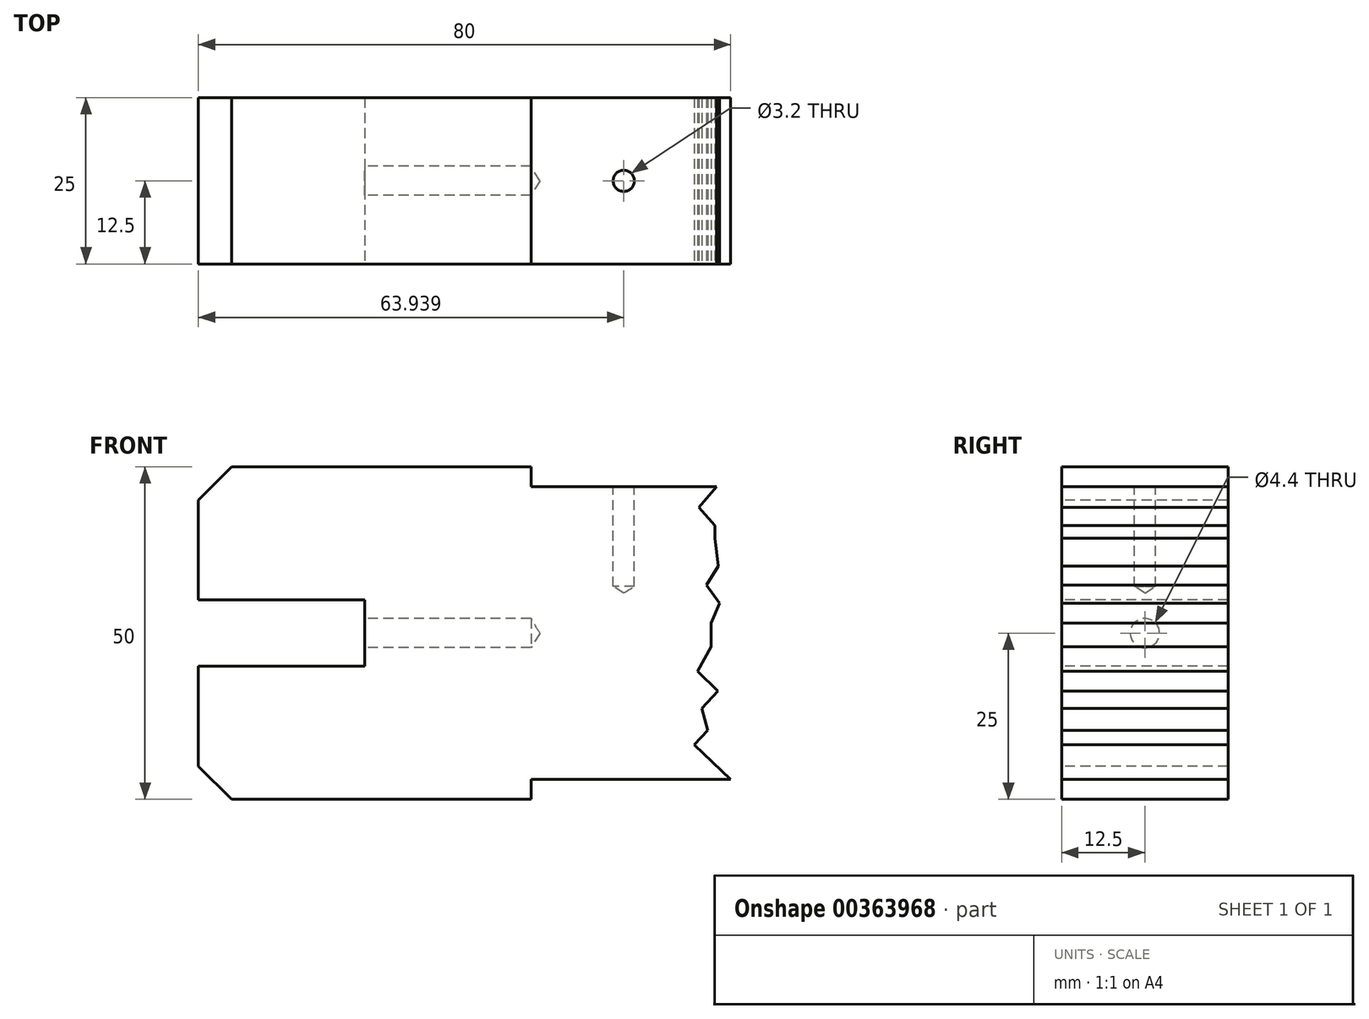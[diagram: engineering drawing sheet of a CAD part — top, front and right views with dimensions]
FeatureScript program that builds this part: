
annotation { "Feature Type Name" : "Feature", "Feature Type Description" : "" }
export const myFeature = defineFeature(function(context is Context, id is Id, definition is map)
    precondition{}
    {
        {
            var Q0;
            Q0=qCreatedBy(makeId("Front.planeOp"),FACE);
            var sketch = newSketch(context, id + "F0", { "sketchPlane" : qUnion([Q0])});
            skLineSegment(sketch, "E0.bottom", {"start": v(40, -25) * mm, "end": v(-40, -25) * mm});
            skLineSegment(sketch, "E0.top", {"start": v(40, 25) * mm, "end": v(-40, 25) * mm});
            skLineSegment(sketch, "E0.left", {"start": v(40, -25) * mm, "end": v(40, 25) * mm});
            skLineSegment(sketch, "E0.right", {"start": v(-40, -25) * mm, "end": v(-40, 25) * mm});
            skPoint(sketch, "E0.middle", {"position": v(0, 0) * mm});
            skSolve(sketch);
        }
        {
            var Q0;
            Q0=makeQuery(id+"F0.imprint","IMPRINT",FACE,{"disambiguationData":[TD([[makeQuery(id+"F0.imprint","IMPRINT",EDGE,{"derivedFrom":sQuery(id+"F0.wireOp",EDGE,"E0.bottom")}),-1.0]])]});
            extrude(context, id + "F1", {"entities" : qUnion([Q0]), "depth" : 25 * mm});
        }
        {
            var Q0;
            Q0=makeQuery(id+"F1.opExtrude","CAP_FACE",FACE,{"disambiguationData":[OSD([sQuery(id+"F0.wireOp",EDGE,"E0.bottom"),sQuery(id+"F0.wireOp",EDGE,"E0.top"),sQuery(id+"F0.wireOp",EDGE,"E0.left"),sQuery(id+"F0.wireOp",EDGE,"E0.right")])],"isStart":false});
            var sketch = newSketch(context, id + "F2", { "sketchPlane" : qUnion([Q0])});
            skLineSegment(sketch, "E1", {"start": v(-35, 25) * mm, "end": v(-40, 20) * mm});
            skLineSegment(sketch, "E2", {"start": v(-40, 20) * mm, "end": v(-40, 25) * mm});
            skLineSegment(sketch, "E3", {"start": v(-40, 25) * mm, "end": v(-35, 25) * mm});
            skLineSegment(sketch, "E4", {"start": v(-35, -25) * mm, "end": v(-40, -25) * mm});
            skLineSegment(sketch, "E5", {"start": v(-40, -25) * mm, "end": v(-40, -20) * mm});
            skLineSegment(sketch, "E6", {"start": v(-40, -20) * mm, "end": v(-35, -25) * mm});
            skSolve(sketch);
        }
        {
            var Q0;
            Q0=makeQuery(id+"F2.imprint","IMPRINT",FACE,{"disambiguationData":[TD([[makeQuery(id+"F2.imprint","IMPRINT",EDGE,{"derivedFrom":sQuery(id+"F2.wireOp",EDGE,"E4")}),-1.0]])]});
            var Q1;
            Q1=makeQuery(id+"F2.imprint","IMPRINT",FACE,{"disambiguationData":[TD([[makeQuery(id+"F2.imprint","IMPRINT",EDGE,{"derivedFrom":sQuery(id+"F2.wireOp",EDGE,"E1")}),-1.0]])]});
            extrude(context, id + "F3", {"entities" : qUnion([Q0, Q1]), "operationType" : NewBodyOperationType.REMOVE, "oppositeDirection" : true, "depth" : 25 * mm});
        }
        {
            var Q0;
            Q0=makeQuery(id+"F1.opExtrude","CAP_FACE",FACE,{"disambiguationData":[OSD([sQuery(id+"F0.wireOp",EDGE,"E0.bottom"),sQuery(id+"F0.wireOp",EDGE,"E0.top"),sQuery(id+"F0.wireOp",EDGE,"E0.left"),sQuery(id+"F0.wireOp",EDGE,"E0.right")])],"isStart":false});
            var sketch = newSketch(context, id + "F4", { "sketchPlane" : qUnion([Q0])});
            skLineSegment(sketch, "E7", {"start": v(-40, 5) * mm, "end": v(-15, 5) * mm});
            skLineSegment(sketch, "E8", {"start": v(-15, 5) * mm, "end": v(-15, -5) * mm});
            skLineSegment(sketch, "E9", {"start": v(-15, -5) * mm, "end": v(-40, -5) * mm});
            skLineSegment(sketch, "E10", {"start": v(-40, -5) * mm, "end": v(-40, 5) * mm});
            skSolve(sketch);
        }
        {
            var Q0;
            Q0=makeQuery(id+"F4.imprint","IMPRINT",FACE,{"disambiguationData":[TD([[makeQuery(id+"F4.imprint","IMPRINT",EDGE,{"derivedFrom":sQuery(id+"F4.wireOp",EDGE,"E7")}),-1.0]])]});
            extrude(context, id + "F5", {"entities" : qUnion([Q0]), "operationType" : NewBodyOperationType.REMOVE, "oppositeDirection" : true, "depth" : 25 * mm});
        }
        {
            var Q0;
            Q0=makeQuery(id+"F5.boolean.opBoolean","COPY",FACE,{"derivedFrom":makeQuery(id+"F5.opExtrude","SWEPT_FACE",FACE,{"disambiguationData":[OSD([sQuery(id+"F4.wireOp",EDGE,"E8")])]})});
            var sketch = newSketch(context, id + "F6", { "sketchPlane" : qUnion([Q0])});
            skPoint(sketch, "E11", {"position": v(12.5, 0) * mm});
            skSolve(sketch);
        }
        {
            var Q0;
            Q0=sQuery(id+"F6.wireOp",VERTEX,"E11");
            var Q1;
            Q1=makeQuery(id+"F1.opExtrude","SWEPT_BODY",BODY,{"disambiguationData":[OSD([sQuery(id+"F0.wireOp",EDGE,"E0.bottom"),sQuery(id+"F0.wireOp",EDGE,"E0.top"),sQuery(id+"F0.wireOp",EDGE,"E0.left"),sQuery(id+"F0.wireOp",EDGE,"E0.right")])]});
            hole(context, id + "F7", {"style" : HoleStyle.SIMPLE, "endStyle" : HoleEndStyle.BLIND, "standardTappedOrClearance" : lookupTablePath({ "fit" : "Normal", "standard" : "ISO", "size" : "M4", "type" : "Clearance" }), "standardBlindInLast" : lookupTablePath({ "fit" : "Standard", "standard" : "ISO", "size" : "M4", "type" : "Clearance" }), "holeDiameter" : 4.4 * mm, "holeDepth" : 25 * mm, "isTappedThrough" : true, "tappedDepth" : 12 * mm, "tapClearance" : 3, "locations" : qUnion([Q0]), "scope" : qUnion([Q1])});
        }
        {
            var Q0;
            Q0=makeQuery(id+"F1.opExtrude","CAP_FACE",FACE,{"disambiguationData":[OSD([sQuery(id+"F0.wireOp",EDGE,"E0.bottom"),sQuery(id+"F0.wireOp",EDGE,"E0.top"),sQuery(id+"F0.wireOp",EDGE,"E0.left"),sQuery(id+"F0.wireOp",EDGE,"E0.right")])],"isStart":false});
            var sketch = newSketch(context, id + "F8", { "sketchPlane" : qUnion([Q0])});
            skLineSegment(sketch, "E12", {"start": v(10, 25) * mm, "end": v(10, 22) * mm});
            skLineSegment(sketch, "E13", {"start": v(10, 22) * mm, "end": v(40, 22) * mm});
            skLineSegment(sketch, "E14", {"start": v(40, 22) * mm, "end": v(40, 25) * mm});
            skLineSegment(sketch, "E15", {"start": v(40, 25) * mm, "end": v(10, 25) * mm});
            skLineSegment(sketch, "E16", {"start": v(10, -25) * mm, "end": v(10, -22) * mm});
            skLineSegment(sketch, "E17", {"start": v(10, -22) * mm, "end": v(40, -22) * mm});
            skLineSegment(sketch, "E18", {"start": v(40, -22) * mm, "end": v(40, -25) * mm});
            skLineSegment(sketch, "E19", {"start": v(40, -25) * mm, "end": v(10, -25) * mm});
            skSolve(sketch);
        }
        {
            var Q0;
            Q0=makeQuery(id+"F8.imprint","IMPRINT",FACE,{"disambiguationData":[TD([[makeQuery(id+"F8.imprint","IMPRINT",EDGE,{"derivedFrom":sQuery(id+"F8.wireOp",EDGE,"E16")}),-1.0]])]});
            var Q1;
            Q1=makeQuery(id+"F8.imprint","IMPRINT",FACE,{"disambiguationData":[TD([[makeQuery(id+"F8.imprint","IMPRINT",EDGE,{"derivedFrom":sQuery(id+"F8.wireOp",EDGE,"E12")}),1.0]])]});
            extrude(context, id + "F9", {"entities" : qUnion([Q0, Q1]), "operationType" : NewBodyOperationType.REMOVE, "oppositeDirection" : true, "depth" : 25 * mm});
        }
        {
            var Q0;
            Q0=makeQuery(id+"F1.opExtrude","CAP_FACE",FACE,{"disambiguationData":[OSD([sQuery(id+"F0.wireOp",EDGE,"E0.bottom"),sQuery(id+"F0.wireOp",EDGE,"E0.top"),sQuery(id+"F0.wireOp",EDGE,"E0.left"),sQuery(id+"F0.wireOp",EDGE,"E0.right")])],"isStart":false});
            var sketch = newSketch(context, id + "F10", { "sketchPlane" : qUnion([Q0])});
            skLineSegment(sketch, "E20", {"start": v(40, -22) * mm, "end": v(34.5, -16.8) * mm});
            skLineSegment(sketch, "E21", {"start": v(34.5, -16.8) * mm, "end": v(34.5, -16.8) * mm});
            skLineSegment(sketch, "E22", {"start": v(34.5, -16.8) * mm, "end": v(36.56, -14.63) * mm});
            skLineSegment(sketch, "E23", {"start": v(36.56, -14.63) * mm, "end": v(35.66, -11.33) * mm});
            skLineSegment(sketch, "E24", {"start": v(35.66, -11.33) * mm, "end": v(38.11, -8.7) * mm});
            skLineSegment(sketch, "E25", {"start": v(38.11, -8.7) * mm, "end": v(35.07, -5.71) * mm});
            skLineSegment(sketch, "E26", {"start": v(35.07, -5.71) * mm, "end": v(37.06, -2.06) * mm});
            skLineSegment(sketch, "E27", {"start": v(37.06, -2.06) * mm, "end": v(37.06, 1.48) * mm});
            skLineSegment(sketch, "E28", {"start": v(37.06, 1.48) * mm, "end": v(38.32, 4.5) * mm});
            skLineSegment(sketch, "E29", {"start": v(38.32, 4.5) * mm, "end": v(36.35, 7.24) * mm});
            skLineSegment(sketch, "E30", {"start": v(36.35, 7.24) * mm, "end": v(38.12, 10.1) * mm});
            skLineSegment(sketch, "E31", {"start": v(38.12, 10.1) * mm, "end": v(37.64, 14.28) * mm});
            skLineSegment(sketch, "E32", {"start": v(37.64, 14.28) * mm, "end": v(37.64, 16.14) * mm});
            skLineSegment(sketch, "E33", {"start": v(37.64, 16.14) * mm, "end": v(35.2, 18.92) * mm});
            skLineSegment(sketch, "E34", {"start": v(35.2, 18.92) * mm, "end": v(37.88, 22) * mm});
            skLineSegment(sketch, "E35", {"start": v(37.88, 22) * mm, "end": v(40, 22) * mm});
            skLineSegment(sketch, "E36", {"start": v(40, 22) * mm, "end": v(40, -22) * mm});
            skSolve(sketch);
        }
        {
            var Q0;
            Q0=makeQuery(id+"F10.imprint","IMPRINT",FACE,{"disambiguationData":[TD([[makeQuery(id+"F10.imprint","IMPRINT",EDGE,{"derivedFrom":sQuery(id+"F10.wireOp",EDGE,"E20")}),-1.0]])]});
            extrude(context, id + "F11", {"entities" : qUnion([Q0]), "operationType" : NewBodyOperationType.REMOVE, "oppositeDirection" : true, "depth" : 25 * mm});
        }
        {
            var Q0;
            Q0=makeQuery(id+"F9.boolean.opBoolean","COPY",FACE,{"derivedFrom":makeQuery(id+"F9.opExtrude","SWEPT_FACE",FACE,{"disambiguationData":[OSD([sQuery(id+"F8.wireOp",EDGE,"E13")])]})});
            var sketch = newSketch(context, id + "F12", { "sketchPlane" : qUnion([Q0])});
            skPoint(sketch, "E37", {"position": v(23.94, -12.5) * mm});
            skPoint(sketch, "E37.positionSnap0", {"position": v(10, -12.5) * mm});
            skPoint(sketch, "E37.positionSnap1", {"position": v(23.94, -25) * mm});
            skSolve(sketch);
        }
        {
            var Q0;
            Q0=sQuery(id+"F12.wireOp",VERTEX,"E37");
            var Q1;
            Q1=makeQuery(id+"F1.opExtrude","SWEPT_BODY",BODY,{"disambiguationData":[OSD([sQuery(id+"F0.wireOp",EDGE,"E0.bottom"),sQuery(id+"F0.wireOp",EDGE,"E0.top"),sQuery(id+"F0.wireOp",EDGE,"E0.left"),sQuery(id+"F0.wireOp",EDGE,"E0.right")])]});
            hole(context, id + "F13", {"style" : HoleStyle.SIMPLE, "endStyle" : HoleEndStyle.BLIND, "standardTappedOrClearance" : lookupTablePath({ "fit" : "Normal", "standard" : "ISO", "engagement" : "75%", "pitch" : "0.75 mm", "size" : "M4", "type" : "Tapped" }), "standardBlindInLast" : lookupTablePath({ "fit" : "Standard", "standard" : "ISO", "engagement" : "75%", "pitch" : "0.75 mm", "size" : "M4", "type" : "Tapped" }), "holeDiameter" : 3.2 * mm, "showTappedDepth" : true, "holeDepth" : 15 * mm, "isTappedThrough" : true, "tappedDepth" : 12.75 * mm, "tapClearance" : 3, "locations" : qUnion([Q0]), "scope" : qUnion([Q1])});
        }
    });
